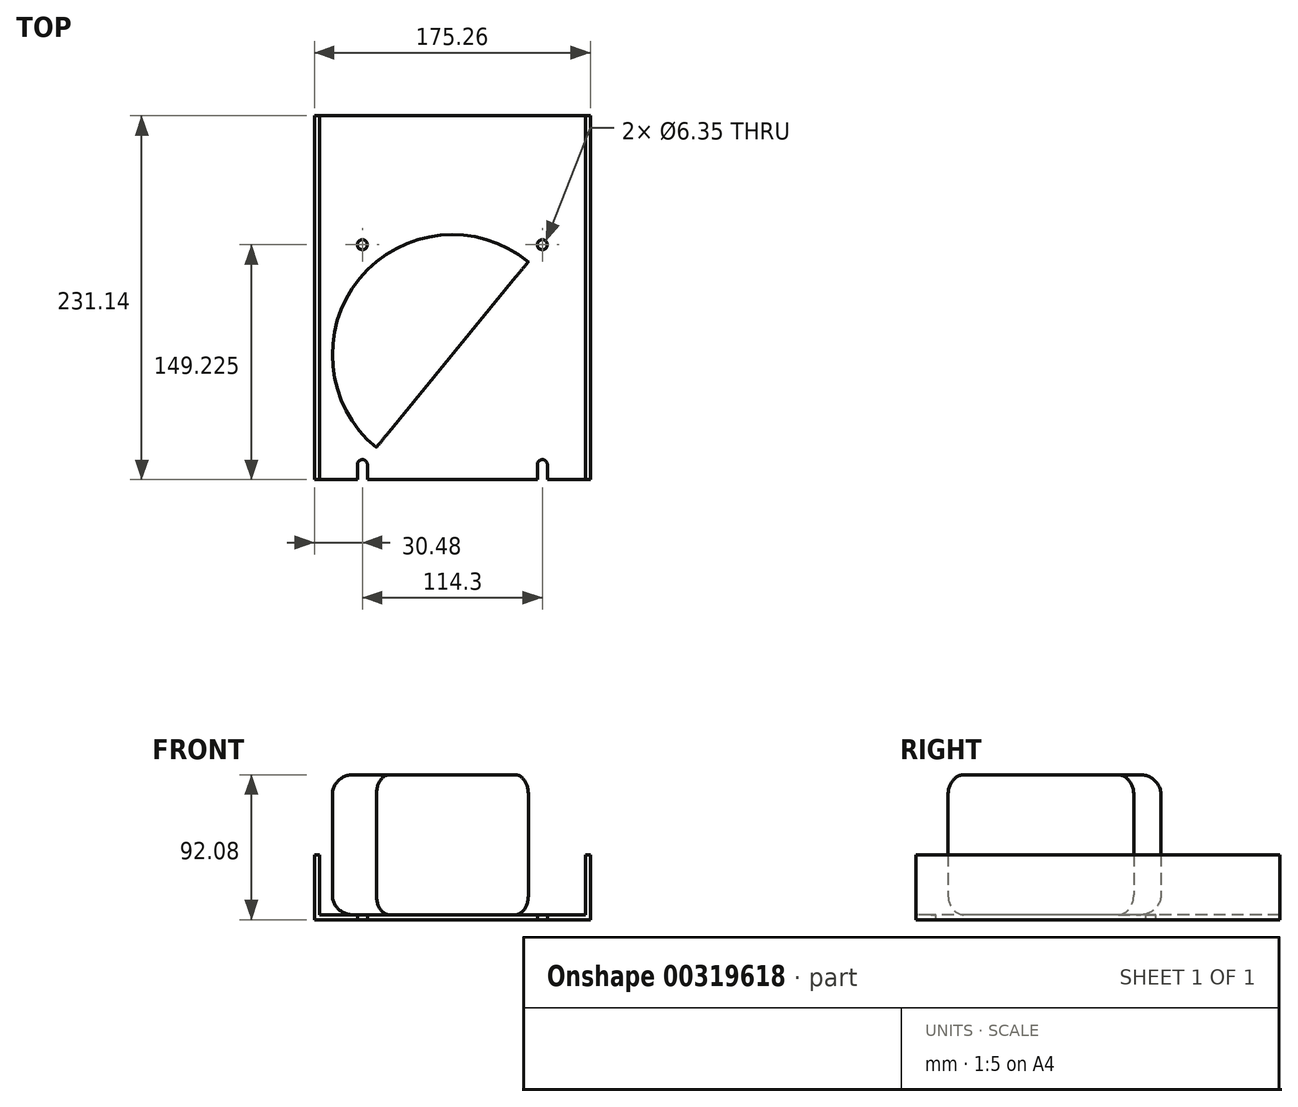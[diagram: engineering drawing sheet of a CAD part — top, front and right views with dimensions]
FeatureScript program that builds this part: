
annotation { "Feature Type Name" : "Feature", "Feature Type Description" : "" }
export const myFeature = defineFeature(function(context is Context, id is Id, definition is map)
    precondition{}
    {
        {
            var Q0;
            Q0=qCreatedBy(makeId("Top.planeOp"),FACE);
            var sketch = newSketch(context, id + "F0", { "sketchPlane" : qUnion([Q0])});
            skLineSegment(sketch, "E0.bottom", {"start": v(0, 0) * mm, "end": v(175.26, 0) * mm});
            skLineSegment(sketch, "E0.top", {"start": v(0, -231.14) * mm, "end": v(27.3, -231.14) * mm});
            skLineSegment(sketch, "E0.left", {"start": v(0, 0) * mm, "end": v(0, -231.14) * mm});
            skLineSegment(sketch, "E0.right", {"start": v(175.26, 0) * mm, "end": v(175.26, -231.14) * mm});
            skLineSegment(sketch, "E1", {"start": v(87.63, -221.62) * mm, "end": v(87.63, -81.91) * mm});
            skLineSegment(sketch, "E2.0", {"start": v(30.48, -81.91) * mm, "end": v(144.78, -81.91) * mm});
            skLineSegment(sketch, "E3.0", {"start": v(144.78, -221.62) * mm, "end": v(144.78, -81.91) * mm});
            skLineSegment(sketch, "E4.0", {"start": v(30.48, -221.62) * mm, "end": v(30.48, -81.91) * mm});
            skLineSegment(sketch, "E5.0", {"start": v(33.66, -221.62) * mm, "end": v(141.6, -221.62) * mm});
            skCircle(sketch, "E6", {"center": v(30.48, -81.91) * mm, "radius": 3.18 * mm});
            skCircle(sketch, "E7", {"center": v(144.78, -81.91) * mm, "radius": 3.18 * mm});
            skPoint(sketch, "E8.orphan", {"position": v(87.63, 0) * mm});
            skPoint(sketch, "E9.orphan", {"position": v(87.63, -231.14) * mm});
            skLineSegment(sketch, "E10", {"start": v(33.66, -221.62) * mm, "end": v(33.66, -231.14) * mm});
            skLineSegment(sketch, "E11", {"start": v(141.6, -221.62) * mm, "end": v(141.6, -231.14) * mm});
            skLineSegment(sketch, "E12", {"start": v(27.3, -221.62) * mm, "end": v(27.3, -231.14) * mm});
            skLineSegment(sketch, "E13", {"start": v(147.96, -221.62) * mm, "end": v(147.96, -231.14) * mm});
            skArc(sketch, "E14", {"start": v(147.96, -221.62) * mm, "mid": v(144.78, -218.44) * mm, "end": v(141.6, -221.62) * mm});
            skArc(sketch, "E15", {"start": v(33.66, -221.62) * mm, "mid": v(30.48, -218.44) * mm, "end": v(27.3, -221.62) * mm});
            skLineSegment(sketch, "E16.0", {"start": v(172.09, 0) * mm, "end": v(172.09, -231.14) * mm});
            skLineSegment(sketch, "E17.0", {"start": v(3.17, 0) * mm, "end": v(3.18, -231.14) * mm});
            skLineSegment(sketch, "E18.trimOffspring", {"start": v(33.66, -231.14) * mm, "end": v(141.6, -231.14) * mm});
            skLineSegment(sketch, "E19.trimOffspring", {"start": v(147.96, -231.14) * mm, "end": v(175.26, -231.14) * mm});
            skSolve(sketch);
        }
        {
            var Q0;
            {var subQ0=sQuery(id+"F0.wireOp",EDGE,"E12");Q0=makeQuery(id+"F0.imprint","IMPRINT",FACE,{"disambiguationData":[TD([[makeQuery(id+"F0.imprint","IMPRINT",EDGE,{"derivedFrom":subQ0}),-1.0]])]});}
            var Q1;
            {var subQ1=sQuery(id+"F0.wireOp",EDGE,"E1");Q1=makeQuery(id+"F0.imprint","IMPRINT",FACE,{"disambiguationData":[TD([[makeQuery(id+"F0.imprint","IMPRINT",EDGE,{"derivedFrom":subQ1}),1.0]])]});}
            var Q2;
            {var subQ1=sQuery(id+"F0.wireOp",EDGE,"E1");Q2=makeQuery(id+"F0.imprint","IMPRINT",FACE,{"disambiguationData":[TD([[makeQuery(id+"F0.imprint","IMPRINT",EDGE,{"derivedFrom":subQ1}),-1.0]])]});}
            var Q3;
            {var subQ0=sQuery(id+"F0.wireOp",EDGE,"E0.left");Q3=makeQuery(id+"F0.imprint","IMPRINT",FACE,{"disambiguationData":[TD([[makeQuery(id+"F0.imprint","IMPRINT",EDGE,{"derivedFrom":subQ0}),1.0]])]});}
            var Q4;
            {var subQ0=sQuery(id+"F0.wireOp",EDGE,"E0.right");Q4=makeQuery(id+"F0.imprint","IMPRINT",FACE,{"disambiguationData":[TD([[makeQuery(id+"F0.imprint","IMPRINT",EDGE,{"derivedFrom":subQ0}),-1.0]])]});}
            var Q5;
            {var subQ0=sQuery(id+"F0.wireOp",EDGE,"E10");Q5=makeQuery(id+"F0.imprint","IMPRINT",FACE,{"disambiguationData":[TD([[makeQuery(id+"F0.imprint","IMPRINT",EDGE,{"derivedFrom":subQ0}),1.0]])]});}
            extrude(context, id + "F1", {"entities" : qUnion([Q0, Q1, Q2, Q3, Q4, Q5]), "oppositeDirection" : true, "depth" : 3.17 * mm});
        }
        {
            var Q0;
            {var subQ0=sQuery(id+"F0.wireOp",EDGE,"E0.left");Q0=makeQuery(id+"F0.imprint","IMPRINT",FACE,{"disambiguationData":[TD([[makeQuery(id+"F0.imprint","IMPRINT",EDGE,{"derivedFrom":subQ0}),1.0]])]});}
            var Q1;
            {var subQ0=sQuery(id+"F0.wireOp",EDGE,"E0.right");Q1=makeQuery(id+"F0.imprint","IMPRINT",FACE,{"disambiguationData":[TD([[makeQuery(id+"F0.imprint","IMPRINT",EDGE,{"derivedFrom":subQ0}),-1.0]])]});}
            extrude(context, id + "F2", {"entities" : qUnion([Q0, Q1]), "operationType" : NewBodyOperationType.ADD, "depth" : 38.1 * mm});
        }
        {
            var Q0;
            Q0=makeQuery(id+"F1.opExtrude","CAP_FACE",FACE,{"disambiguationData":[OSD([sQuery(id+"F0.wireOp",EDGE,"E0.bottom"),sQuery(id+"F0.wireOp",EDGE,"E0.top"),sQuery(id+"F0.wireOp",EDGE,"E0.left"),sQuery(id+"F0.wireOp",EDGE,"E0.right"),sQuery(id+"F0.wireOp",EDGE,"E6"),sQuery(id+"F0.wireOp",EDGE,"E7"),sQuery(id+"F0.wireOp",EDGE,"E10"),sQuery(id+"F0.wireOp",EDGE,"E11"),sQuery(id+"F0.wireOp",EDGE,"E12"),sQuery(id+"F0.wireOp",EDGE,"E13"),sQuery(id+"F0.wireOp",EDGE,"E14"),sQuery(id+"F0.wireOp",EDGE,"E15"),sQuery(id+"F0.wireOp",EDGE,"E18.trimOffspring"),sQuery(id+"F0.wireOp",EDGE,"E19.trimOffspring")])],"isStart":true});
            var sketch = newSketch(context, id + "F3", { "sketchPlane" : qUnion([Q0])});
            skCircle(sketch, "E20.0", {"center": v(30.48, -81.91) * mm, "radius": 3.18 * mm});
            skCircle(sketch, "E21.0", {"center": v(144.78, -81.91) * mm, "radius": 3.18 * mm});
            skArc(sketch, "E22.0", {"start": v(33.66, -221.62) * mm, "mid": v(30.48, -218.44) * mm, "end": v(27.3, -221.62) * mm});
            skArc(sketch, "E23.0", {"start": v(147.96, -221.62) * mm, "mid": v(144.78, -218.44) * mm, "end": v(141.6, -221.62) * mm});
            skLineSegment(sketch, "E24", {"start": v(30.48, -81.91) * mm, "end": v(144.78, -221.62) * mm});
            skLineSegment(sketch, "E25", {"start": v(144.78, -81.91) * mm, "end": v(30.48, -221.62) * mm});
            skCircle(sketch, "E26", {"center": v(87.63, -151.76) * mm, "radius": 25.4 * mm});
            skCircle(sketch, "E27", {"center": v(87.63, -151.76) * mm, "radius": 76.2 * mm});
            skSolve(sketch);
        }
        {
            var Q0;
            {var subQ0=sQuery(id+"F3.wireOp",EDGE,"E27");var subQ1=sQuery(id+"F3.wireOp",EDGE,"E24");var subQ2=makeQuery(id+"F3.imprint","INTERSECT",VERTEX,{"disambiguationData":[OD(0.0)],"derivedFrom":[subQ1,subQ0]});Q0=makeQuery(id+"F3.imprint","IMPRINT",FACE,{"disambiguationData":[TD([[makeQuery(id+"F3.imprint","IMPRINT",EDGE,{"disambiguationData":[TD([[subQ2,-1.0]])],"derivedFrom":subQ1}),-1.0]])]});}
            var Q1;
            {var subQ0=sQuery(id+"F3.wireOp",EDGE,"E27");var subQ1=sQuery(id+"F3.wireOp",EDGE,"E24");var subQ2=makeQuery(id+"F3.imprint","INTERSECT",VERTEX,{"disambiguationData":[OD(0.0)],"derivedFrom":[subQ1,subQ0]});Q1=makeQuery(id+"F3.imprint","IMPRINT",FACE,{"disambiguationData":[TD([[makeQuery(id+"F3.imprint","IMPRINT",EDGE,{"disambiguationData":[TD([[subQ2,-1.0]])],"derivedFrom":subQ1}),1.0]])]});}
            var Q2;
            {var subQ0=sQuery(id+"F3.wireOp",EDGE,"E26");var subQ1=sQuery(id+"F3.wireOp",EDGE,"E24");var subQ2=makeQuery(id+"F3.imprint","INTERSECT",VERTEX,{"disambiguationData":[OD(1.0)],"derivedFrom":[subQ1,subQ0]});Q2=makeQuery(id+"F3.imprint","IMPRINT",FACE,{"disambiguationData":[TD([[makeQuery(id+"F3.imprint","IMPRINT",EDGE,{"disambiguationData":[TD([[subQ2,-1.0]])],"derivedFrom":subQ1}),1.0]])]});}
            var Q3;
            {var subQ0=sQuery(id+"F3.wireOp",EDGE,"E26");var subQ5=sQuery(id+"F3.wireOp",EDGE,"E24");var subQ6=makeQuery(id+"F3.imprint","INTERSECT",VERTEX,{"disambiguationData":[OD(1.0)],"derivedFrom":[subQ5,subQ0]});Q3=makeQuery(id+"F3.imprint","IMPRINT",FACE,{"disambiguationData":[TD([[makeQuery(id+"F3.imprint","IMPRINT",EDGE,{"disambiguationData":[TD([[subQ6,-1.0]])],"derivedFrom":subQ5}),-1.0]])]});}
            extrude(context, id + "F4", {"entities" : qUnion([Q0, Q1, Q2, Q3]), "depth" : 88.9 * mm});
        }
        {
            var Q0;
            Q0=makeQuery(id+"F4.opExtrude","CAP_EDGE",EDGE,{"disambiguationData":[OSD([sQuery(id+"F3.wireOp",EDGE,"E27")])],"isStart":false});
            var Q1;
            Q1=makeQuery(id+"F4.opExtrude","CAP_EDGE",EDGE,{"disambiguationData":[OSD([sQuery(id+"F3.wireOp",EDGE,"E26")])],"isStart":false});
            var Q2;
            Q2=makeQuery(id+"F4.opExtrude","CAP_EDGE",EDGE,{"disambiguationData":[OSD([sQuery(id+"F3.wireOp",EDGE,"E27")])],"isStart":true});
            var Q3;
            Q3=makeQuery(id+"F4.opExtrude","CAP_EDGE",EDGE,{"disambiguationData":[OSD([sQuery(id+"F3.wireOp",EDGE,"E26")])],"isStart":true});
            fillet(context, id + "F5", {"entities" : qUnion([Q0, Q1, Q2, Q3]), "radius" : 12.7 * mm, "tangentPropagation" : true, "allowEdgeOverflow" : false});
        }
    });
